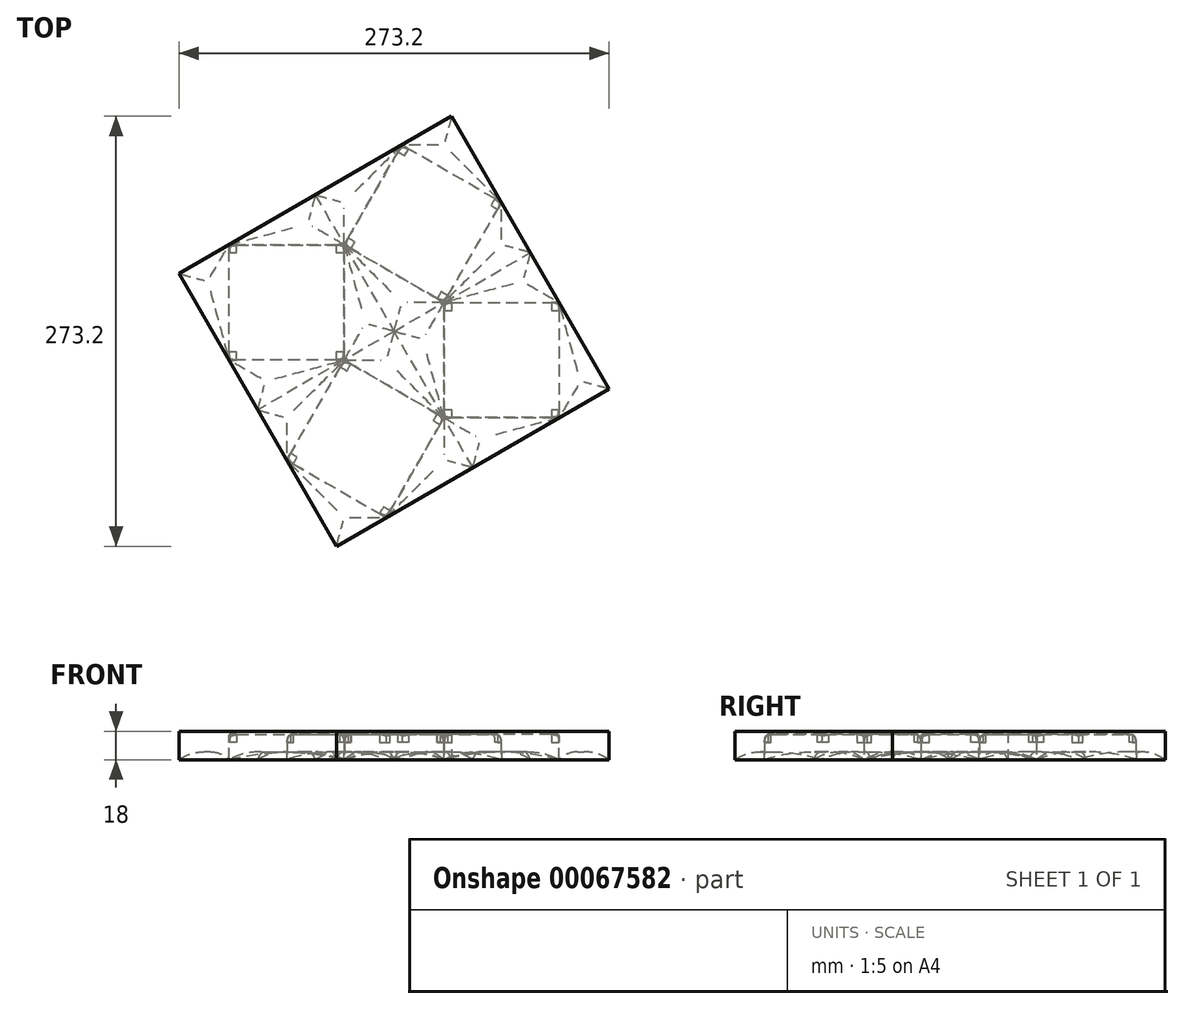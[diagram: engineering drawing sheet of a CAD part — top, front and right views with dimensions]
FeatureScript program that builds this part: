
annotation { "Feature Type Name" : "Feature", "Feature Type Description" : "" }
export const myFeature = defineFeature(function(context is Context, id is Id, definition is map)
    precondition{}
    {
        {
            var Q0;
            Q0=qCreatedBy(makeId("Top.planeOp"),FACE);
            var sketch = newSketch(context, id + "F0", { "sketchPlane" : qUnion([Q0])});
            skLineSegment(sketch, "E0.rect.bottom", {"start": v(36.6, -36.6) * mm, "end": v(-36.6, -36.6) * mm});
            skLineSegment(sketch, "E0.rect.top", {"start": v(36.6, 36.6) * mm, "end": v(-36.6, 36.6) * mm});
            skLineSegment(sketch, "E0.rect.left", {"start": v(36.6, -36.6) * mm, "end": v(36.6, 36.6) * mm});
            skLineSegment(sketch, "E0.rect.right", {"start": v(-36.6, -36.6) * mm, "end": v(-36.6, 36.6) * mm});
            skPoint(sketch, "E0.rect.middle", {"position": v(0, 0) * mm});
            skLineSegment(sketch, "E1", {"start": v(36.6, 36.6) * mm, "end": v(68.3, -18.3) * mm});
            skLineSegment(sketch, "E2", {"start": v(68.3, -18.3) * mm, "end": v(36.6, -36.6) * mm});
            skLineSegment(sketch, "E3.1.0", {"start": v(18.3, 68.3) * mm, "end": v(36.6, 36.6) * mm});
            skLineSegment(sketch, "E3.1.1", {"start": v(-36.6, 36.6) * mm, "end": v(18.3, 68.3) * mm});
            skLineSegment(sketch, "E3.2.0", {"start": v(-68.3, 18.3) * mm, "end": v(-36.6, 36.6) * mm});
            skLineSegment(sketch, "E3.2.1", {"start": v(-36.6, -36.6) * mm, "end": v(-68.3, 18.3) * mm});
            skLineSegment(sketch, "E3.3.0", {"start": v(-18.3, -68.3) * mm, "end": v(-36.6, -36.6) * mm});
            skLineSegment(sketch, "E3.3.1", {"start": v(36.6, -36.6) * mm, "end": v(-18.3, -68.3) * mm});
            skSolve(sketch);
        }
        {
            var Q0;
            Q0=makeQuery(id+"F0.imprint","IMPRINT",FACE,{"disambiguationData":[TD([[makeQuery(id+"F0.imprint","IMPRINT",EDGE,{"derivedFrom":sQuery(id+"F0.wireOp",EDGE,"E0.rect.bottom")}),-1.0]])]});
            extrude(context, id + "F1", {"entities" : qUnion([Q0]), "depth" : 16 * mm});
        }
        {
            var Q0;
            Q0=makeQuery(id+"F0.imprint","IMPRINT",FACE,{"disambiguationData":[TD([[makeQuery(id+"F0.imprint","IMPRINT",EDGE,{"derivedFrom":sQuery(id+"F0.wireOp",EDGE,"E0.rect.right")}),1.0]])]});
            var Q1;
            Q1=makeQuery(id+"F0.imprint","IMPRINT",FACE,{"disambiguationData":[TD([[makeQuery(id+"F0.imprint","IMPRINT",EDGE,{"derivedFrom":sQuery(id+"F0.wireOp",EDGE,"E0.rect.top")}),-1.0]])]});
            var Q2;
            Q2=makeQuery(id+"F0.imprint","IMPRINT",FACE,{"disambiguationData":[TD([[makeQuery(id+"F0.imprint","IMPRINT",EDGE,{"derivedFrom":sQuery(id+"F0.wireOp",EDGE,"E0.rect.left")}),-1.0]])]});
            var Q3;
            Q3=makeQuery(id+"F0.imprint","IMPRINT",FACE,{"disambiguationData":[TD([[makeQuery(id+"F0.imprint","IMPRINT",EDGE,{"derivedFrom":sQuery(id+"F0.wireOp",EDGE,"E0.rect.bottom")}),1.0]])]});
            extrude(context, id + "F2", {"entities" : qUnion([Q0, Q1, Q2, Q3]), "depth" : 5 * mm});
        }
        {
            var Q0;
            Q0=makeQuery(id+"F2.opExtrude","CAP_FACE",FACE,{"disambiguationData":[OSD([sQuery(id+"F0.wireOp",EDGE,"E0.rect.right"),sQuery(id+"F0.wireOp",EDGE,"E3.2.0"),sQuery(id+"F0.wireOp",EDGE,"E3.2.1")])],"isStart":false});
            var Q1;
            Q1=makeQuery(id+"F2.opExtrude","CAP_FACE",FACE,{"disambiguationData":[OSD([sQuery(id+"F0.wireOp",EDGE,"E0.rect.top"),sQuery(id+"F0.wireOp",EDGE,"E3.1.0"),sQuery(id+"F0.wireOp",EDGE,"E3.1.1")])],"isStart":false});
            var Q2;
            Q2=makeQuery(id+"F2.opExtrude","CAP_FACE",FACE,{"disambiguationData":[OSD([sQuery(id+"F0.wireOp",EDGE,"E0.rect.left"),sQuery(id+"F0.wireOp",EDGE,"E1"),sQuery(id+"F0.wireOp",EDGE,"E2")])],"isStart":false});
            var Q3;
            Q3=makeQuery(id+"F2.opExtrude","CAP_FACE",FACE,{"disambiguationData":[OSD([sQuery(id+"F0.wireOp",EDGE,"E0.rect.bottom"),sQuery(id+"F0.wireOp",EDGE,"E3.3.0"),sQuery(id+"F0.wireOp",EDGE,"E3.3.1")])],"isStart":false});
            fillet(context, id + "F3", {"entities" : qUnion([Q0, Q1, Q2, Q3]), "radius" : 16.26 * mm, "tangentPropagation" : true, "allowEdgeOverflow" : false});
        }
        {
            var Q0;
            Q0=makeQuery(id+"F1.opExtrude","CAP_EDGE",EDGE,{"disambiguationData":[OSD([sQuery(id+"F0.wireOp",EDGE,"E0.rect.bottom")])],"isStart":false});
            var Q1;
            Q1=makeQuery(id+"F1.opExtrude","CAP_EDGE",EDGE,{"disambiguationData":[OSD([sQuery(id+"F0.wireOp",EDGE,"E0.rect.right")])],"isStart":false});
            var Q2;
            Q2=makeQuery(id+"F1.opExtrude","CAP_EDGE",EDGE,{"disambiguationData":[OSD([sQuery(id+"F0.wireOp",EDGE,"E0.rect.top")])],"isStart":false});
            var Q3;
            Q3=makeQuery(id+"F1.opExtrude","CAP_EDGE",EDGE,{"disambiguationData":[OSD([sQuery(id+"F0.wireOp",EDGE,"E0.rect.left")])],"isStart":false});
            var Q4;
            Q4=makeQuery(id+"F1.opExtrude","SWEPT_EDGE",EDGE,{"disambiguationData":[OSD([sQuery(id+"F0.wireOp",EDGE,"E0.rect.bottom"),sQuery(id+"F0.wireOp",EDGE,"E0.rect.left"),sQuery(id+"F0.wireOp",EDGE,"E2"),sQuery(id+"F0.wireOp",EDGE,"E3.3.1")])]});
            var Q5;
            Q5=makeQuery(id+"F1.opExtrude","SWEPT_EDGE",EDGE,{"disambiguationData":[OSD([sQuery(id+"F0.wireOp",EDGE,"E0.rect.bottom"),sQuery(id+"F0.wireOp",EDGE,"E0.rect.right"),sQuery(id+"F0.wireOp",EDGE,"E3.2.1"),sQuery(id+"F0.wireOp",EDGE,"E3.3.0")])]});
            var Q6;
            Q6=makeQuery(id+"F1.opExtrude","SWEPT_EDGE",EDGE,{"disambiguationData":[OSD([sQuery(id+"F0.wireOp",EDGE,"E0.rect.top"),sQuery(id+"F0.wireOp",EDGE,"E0.rect.right"),sQuery(id+"F0.wireOp",EDGE,"E3.1.1"),sQuery(id+"F0.wireOp",EDGE,"E3.2.0")])]});
            var Q7;
            Q7=makeQuery(id+"F1.opExtrude","SWEPT_EDGE",EDGE,{"disambiguationData":[OSD([sQuery(id+"F0.wireOp",EDGE,"E0.rect.top"),sQuery(id+"F0.wireOp",EDGE,"E0.rect.left"),sQuery(id+"F0.wireOp",EDGE,"E1"),sQuery(id+"F0.wireOp",EDGE,"E3.1.0")])]});
            fillet(context, id + "F4", {"entities" : qUnion([Q0, Q1, Q2, Q3, Q4, Q5, Q6, Q7]), "radius" : 5 * mm, "tangentPropagation" : true, "rho" : 0.9, "crossSection" : FilletCrossSection.CONIC, "allowEdgeOverflow" : false});
        }
        {
            var Q0;
            Q0=sQuery(id+"F0.wireOp",EDGE,"E3.3.1");
            cPlane(context, id + "F5", {"entities" : qUnion([Q0]), "cplaneType" : CPlaneType.LINE_ANGLE, "offset" : 150 * mm, "angle" : 0 * degree, "width" : 150 * mm, "height" : 150 * mm});
        }
        {
            var Q0;
            Q0=makeQuery(id+"F1.opExtrude","SWEPT_BODY",BODY,{"disambiguationData":[OSD([sQuery(id+"F0.wireOp",EDGE,"E0.rect.bottom"),sQuery(id+"F0.wireOp",EDGE,"E0.rect.top"),sQuery(id+"F0.wireOp",EDGE,"E0.rect.left"),sQuery(id+"F0.wireOp",EDGE,"E0.rect.right")])]});
            var Q1;
            Q1=makeQuery(id+"F2.opExtrude","SWEPT_BODY",BODY,{"disambiguationData":[OSD([sQuery(id+"F0.wireOp",EDGE,"E0.rect.right"),sQuery(id+"F0.wireOp",EDGE,"E3.2.0"),sQuery(id+"F0.wireOp",EDGE,"E3.2.1")])]});
            var Q2;
            Q2=makeQuery(id+"F2.opExtrude","SWEPT_BODY",BODY,{"disambiguationData":[OSD([sQuery(id+"F0.wireOp",EDGE,"E0.rect.top"),sQuery(id+"F0.wireOp",EDGE,"E3.1.0"),sQuery(id+"F0.wireOp",EDGE,"E3.1.1")])]});
            var Q3;
            Q3=makeQuery(id+"F2.opExtrude","SWEPT_BODY",BODY,{"disambiguationData":[OSD([sQuery(id+"F0.wireOp",EDGE,"E0.rect.left"),sQuery(id+"F0.wireOp",EDGE,"E1"),sQuery(id+"F0.wireOp",EDGE,"E2")])]});
            var Q4;
            Q4=makeQuery(id+"F2.opExtrude","SWEPT_BODY",BODY,{"disambiguationData":[OSD([sQuery(id+"F0.wireOp",EDGE,"E0.rect.bottom"),sQuery(id+"F0.wireOp",EDGE,"E3.3.0"),sQuery(id+"F0.wireOp",EDGE,"E3.3.1")])]});
            var Q5;
            Q5=qCreatedBy(id+"F5.planeOp",FACE);
            mirror(context, id + "F6", {"entities" : qUnion([Q0, Q1, Q2, Q3, Q4]), "mirrorPlane" : qUnion([Q5])});
        }
        {
            var Q0;
            {var subQ0=sQuery(id+"F0.wireOp",EDGE,"E3.1.0");Q0=makeQuery(id+"F6.opPattern","COPY",EDGE,{"derivedFrom":makeQuery(id+"F3.opFillet","BLEND_EDGE",EDGE,{"blendedFrom":[makeQuery(id+"F2.opExtrude","CAP_EDGE",EDGE,{"disambiguationData":[OSD([subQ0])],"isStart":false}),makeQuery(id+"F2.opExtrude","CAP_FACE",FACE,{"disambiguationData":[OSD([sQuery(id+"F0.wireOp",EDGE,"E0.rect.top"),subQ0,sQuery(id+"F0.wireOp",EDGE,"E3.1.1")])],"isStart":true})],"blendedInto":[makeQuery(id+"F2.opExtrude","CAP_FACE",FACE,{"disambiguationData":[OSD([sQuery(id+"F0.wireOp",EDGE,"E0.rect.top"),subQ0,sQuery(id+"F0.wireOp",EDGE,"E3.1.1")])],"isStart":true})]}),"instanceName":"1"});}
            cPlane(context, id + "F7", {"entities" : qUnion([Q0]), "cplaneType" : CPlaneType.LINE_ANGLE, "offset" : 150 * mm, "angle" : 90 * degree, "width" : 150 * mm, "height" : 150 * mm});
        }
        {
            var Q0;
            Q0=makeQuery(id+"F2.opExtrude","SWEPT_BODY",BODY,{"disambiguationData":[OSD([sQuery(id+"F0.wireOp",EDGE,"E0.rect.top"),sQuery(id+"F0.wireOp",EDGE,"E3.1.0"),sQuery(id+"F0.wireOp",EDGE,"E3.1.1")])]});
            var Q1;
            Q1=makeQuery(id+"F2.opExtrude","SWEPT_BODY",BODY,{"disambiguationData":[OSD([sQuery(id+"F0.wireOp",EDGE,"E0.rect.left"),sQuery(id+"F0.wireOp",EDGE,"E1"),sQuery(id+"F0.wireOp",EDGE,"E2")])]});
            var Q2;
            Q2=makeQuery(id+"F6.opPattern","COPY",BODY,{"derivedFrom":makeQuery(id+"F2.opExtrude","SWEPT_BODY",BODY,{"disambiguationData":[OSD([sQuery(id+"F0.wireOp",EDGE,"E0.rect.left"),sQuery(id+"F0.wireOp",EDGE,"E1"),sQuery(id+"F0.wireOp",EDGE,"E2")])]}),"instanceName":"1"});
            var Q3;
            Q3=makeQuery(id+"F6.opPattern","COPY",BODY,{"derivedFrom":makeQuery(id+"F2.opExtrude","SWEPT_BODY",BODY,{"disambiguationData":[OSD([sQuery(id+"F0.wireOp",EDGE,"E0.rect.top"),sQuery(id+"F0.wireOp",EDGE,"E3.1.0"),sQuery(id+"F0.wireOp",EDGE,"E3.1.1")])]}),"instanceName":"1"});
            var Q4;
            Q4=makeQuery(id+"F6.opPattern","COPY",BODY,{"derivedFrom":makeQuery(id+"F1.opExtrude","SWEPT_BODY",BODY,{"disambiguationData":[OSD([sQuery(id+"F0.wireOp",EDGE,"E0.rect.bottom"),sQuery(id+"F0.wireOp",EDGE,"E0.rect.top"),sQuery(id+"F0.wireOp",EDGE,"E0.rect.left"),sQuery(id+"F0.wireOp",EDGE,"E0.rect.right")])]}),"instanceName":"1"});
            var Q5;
            Q5=makeQuery(id+"F1.opExtrude","SWEPT_BODY",BODY,{"disambiguationData":[OSD([sQuery(id+"F0.wireOp",EDGE,"E0.rect.bottom"),sQuery(id+"F0.wireOp",EDGE,"E0.rect.top"),sQuery(id+"F0.wireOp",EDGE,"E0.rect.left"),sQuery(id+"F0.wireOp",EDGE,"E0.rect.right")])]});
            var Q6;
            Q6=makeQuery(id+"F2.opExtrude","SWEPT_BODY",BODY,{"disambiguationData":[OSD([sQuery(id+"F0.wireOp",EDGE,"E0.rect.right"),sQuery(id+"F0.wireOp",EDGE,"E3.2.0"),sQuery(id+"F0.wireOp",EDGE,"E3.2.1")])]});
            var Q7;
            Q7=makeQuery(id+"F2.opExtrude","SWEPT_BODY",BODY,{"disambiguationData":[OSD([sQuery(id+"F0.wireOp",EDGE,"E0.rect.bottom"),sQuery(id+"F0.wireOp",EDGE,"E3.3.0"),sQuery(id+"F0.wireOp",EDGE,"E3.3.1")])]});
            var Q8;
            Q8=makeQuery(id+"F6.opPattern","COPY",BODY,{"derivedFrom":makeQuery(id+"F2.opExtrude","SWEPT_BODY",BODY,{"disambiguationData":[OSD([sQuery(id+"F0.wireOp",EDGE,"E0.rect.bottom"),sQuery(id+"F0.wireOp",EDGE,"E3.3.0"),sQuery(id+"F0.wireOp",EDGE,"E3.3.1")])]}),"instanceName":"1"});
            var Q9;
            Q9=makeQuery(id+"F6.opPattern","COPY",BODY,{"derivedFrom":makeQuery(id+"F2.opExtrude","SWEPT_BODY",BODY,{"disambiguationData":[OSD([sQuery(id+"F0.wireOp",EDGE,"E0.rect.right"),sQuery(id+"F0.wireOp",EDGE,"E3.2.0"),sQuery(id+"F0.wireOp",EDGE,"E3.2.1")])]}),"instanceName":"1"});
            var Q10;
            Q10=qCreatedBy(id+"F7.planeOp",FACE);
            mirror(context, id + "F8", {"entities" : qUnion([Q0, Q1, Q2, Q3, Q4, Q5, Q6, Q7, Q8, Q9]), "mirrorPlane" : qUnion([Q10])});
        }
        {
            var Q0;
            Q0=qCreatedBy(makeId("Top.planeOp"),FACE);
            var sketch = newSketch(context, id + "F9", { "sketchPlane" : qUnion([Q0])});
            skLineSegment(sketch, "E4", {"start": v(-68.3, 18.3) * mm, "end": v(104.9, 118.3) * mm});
            skLineSegment(sketch, "E5", {"start": v(104.9, 118.3) * mm, "end": v(204.9, -54.9) * mm});
            skLineSegment(sketch, "E6", {"start": v(204.9, -54.9) * mm, "end": v(31.7, -154.9) * mm});
            skLineSegment(sketch, "E7", {"start": v(31.7, -154.9) * mm, "end": v(-68.3, 18.3) * mm});
            skSolve(sketch);
        }
        {
            var Q0;
            Q0 = qSketchRegion(id + "F9", true);
            extrude(context, id + "F10", {"entities" : qUnion([Q0]), "depth" : 18 * mm});
        }
        {
            var Q0;
            Q0=makeQuery(id+"F1.opExtrude","SWEPT_BODY",BODY,{"disambiguationData":[OSD([sQuery(id+"F0.wireOp",EDGE,"E0.rect.bottom"),sQuery(id+"F0.wireOp",EDGE,"E0.rect.top"),sQuery(id+"F0.wireOp",EDGE,"E0.rect.left"),sQuery(id+"F0.wireOp",EDGE,"E0.rect.right")])]});
            var Q1;
            Q1=makeQuery(id+"F2.opExtrude","SWEPT_BODY",BODY,{"disambiguationData":[OSD([sQuery(id+"F0.wireOp",EDGE,"E0.rect.bottom"),sQuery(id+"F0.wireOp",EDGE,"E3.3.0"),sQuery(id+"F0.wireOp",EDGE,"E3.3.1")])]});
            var Q2;
            Q2=makeQuery(id+"F2.opExtrude","SWEPT_BODY",BODY,{"disambiguationData":[OSD([sQuery(id+"F0.wireOp",EDGE,"E0.rect.top"),sQuery(id+"F0.wireOp",EDGE,"E3.1.0"),sQuery(id+"F0.wireOp",EDGE,"E3.1.1")])]});
            var Q3;
            Q3=makeQuery(id+"F2.opExtrude","SWEPT_BODY",BODY,{"disambiguationData":[OSD([sQuery(id+"F0.wireOp",EDGE,"E0.rect.left"),sQuery(id+"F0.wireOp",EDGE,"E1"),sQuery(id+"F0.wireOp",EDGE,"E2")])]});
            var Q4;
            Q4=makeQuery(id+"F2.opExtrude","SWEPT_BODY",BODY,{"disambiguationData":[OSD([sQuery(id+"F0.wireOp",EDGE,"E0.rect.right"),sQuery(id+"F0.wireOp",EDGE,"E3.2.0"),sQuery(id+"F0.wireOp",EDGE,"E3.2.1")])]});
            var Q5;
            Q5=makeQuery(id+"F6.opPattern","COPY",BODY,{"derivedFrom":makeQuery(id+"F1.opExtrude","SWEPT_BODY",BODY,{"disambiguationData":[OSD([sQuery(id+"F0.wireOp",EDGE,"E0.rect.bottom"),sQuery(id+"F0.wireOp",EDGE,"E0.rect.top"),sQuery(id+"F0.wireOp",EDGE,"E0.rect.left"),sQuery(id+"F0.wireOp",EDGE,"E0.rect.right")])]}),"instanceName":"1"});
            var Q6;
            Q6=makeQuery(id+"F6.opPattern","COPY",BODY,{"derivedFrom":makeQuery(id+"F2.opExtrude","SWEPT_BODY",BODY,{"disambiguationData":[OSD([sQuery(id+"F0.wireOp",EDGE,"E0.rect.bottom"),sQuery(id+"F0.wireOp",EDGE,"E3.3.0"),sQuery(id+"F0.wireOp",EDGE,"E3.3.1")])]}),"instanceName":"1"});
            var Q7;
            Q7=makeQuery(id+"F6.opPattern","COPY",BODY,{"derivedFrom":makeQuery(id+"F2.opExtrude","SWEPT_BODY",BODY,{"disambiguationData":[OSD([sQuery(id+"F0.wireOp",EDGE,"E0.rect.top"),sQuery(id+"F0.wireOp",EDGE,"E3.1.0"),sQuery(id+"F0.wireOp",EDGE,"E3.1.1")])]}),"instanceName":"1"});
            var Q8;
            Q8=makeQuery(id+"F6.opPattern","COPY",BODY,{"derivedFrom":makeQuery(id+"F2.opExtrude","SWEPT_BODY",BODY,{"disambiguationData":[OSD([sQuery(id+"F0.wireOp",EDGE,"E0.rect.left"),sQuery(id+"F0.wireOp",EDGE,"E1"),sQuery(id+"F0.wireOp",EDGE,"E2")])]}),"instanceName":"1"});
            var Q9;
            Q9=makeQuery(id+"F6.opPattern","COPY",BODY,{"derivedFrom":makeQuery(id+"F2.opExtrude","SWEPT_BODY",BODY,{"disambiguationData":[OSD([sQuery(id+"F0.wireOp",EDGE,"E0.rect.right"),sQuery(id+"F0.wireOp",EDGE,"E3.2.0"),sQuery(id+"F0.wireOp",EDGE,"E3.2.1")])]}),"instanceName":"1"});
            var Q10;
            Q10=makeQuery(id+"F8.opPattern","COPY",BODY,{"derivedFrom":makeQuery(id+"F1.opExtrude","SWEPT_BODY",BODY,{"disambiguationData":[OSD([sQuery(id+"F0.wireOp",EDGE,"E0.rect.bottom"),sQuery(id+"F0.wireOp",EDGE,"E0.rect.top"),sQuery(id+"F0.wireOp",EDGE,"E0.rect.left"),sQuery(id+"F0.wireOp",EDGE,"E0.rect.right")])]}),"instanceName":"1"});
            var Q11;
            Q11=makeQuery(id+"F8.opPattern","COPY",BODY,{"derivedFrom":makeQuery(id+"F2.opExtrude","SWEPT_BODY",BODY,{"disambiguationData":[OSD([sQuery(id+"F0.wireOp",EDGE,"E0.rect.bottom"),sQuery(id+"F0.wireOp",EDGE,"E3.3.0"),sQuery(id+"F0.wireOp",EDGE,"E3.3.1")])]}),"instanceName":"1"});
            var Q12;
            Q12=makeQuery(id+"F8.opPattern","COPY",BODY,{"derivedFrom":makeQuery(id+"F2.opExtrude","SWEPT_BODY",BODY,{"disambiguationData":[OSD([sQuery(id+"F0.wireOp",EDGE,"E0.rect.top"),sQuery(id+"F0.wireOp",EDGE,"E3.1.0"),sQuery(id+"F0.wireOp",EDGE,"E3.1.1")])]}),"instanceName":"1"});
            var Q13;
            Q13=makeQuery(id+"F8.opPattern","COPY",BODY,{"derivedFrom":makeQuery(id+"F2.opExtrude","SWEPT_BODY",BODY,{"disambiguationData":[OSD([sQuery(id+"F0.wireOp",EDGE,"E0.rect.left"),sQuery(id+"F0.wireOp",EDGE,"E1"),sQuery(id+"F0.wireOp",EDGE,"E2")])]}),"instanceName":"1"});
            var Q14;
            Q14=makeQuery(id+"F8.opPattern","COPY",BODY,{"derivedFrom":makeQuery(id+"F2.opExtrude","SWEPT_BODY",BODY,{"disambiguationData":[OSD([sQuery(id+"F0.wireOp",EDGE,"E0.rect.right"),sQuery(id+"F0.wireOp",EDGE,"E3.2.0"),sQuery(id+"F0.wireOp",EDGE,"E3.2.1")])]}),"instanceName":"1"});
            var Q15;
            Q15=makeQuery(id+"F8.opPattern","COPY",BODY,{"derivedFrom":makeQuery(id+"F6.opPattern","COPY",BODY,{"derivedFrom":makeQuery(id+"F1.opExtrude","SWEPT_BODY",BODY,{"disambiguationData":[OSD([sQuery(id+"F0.wireOp",EDGE,"E0.rect.bottom"),sQuery(id+"F0.wireOp",EDGE,"E0.rect.top"),sQuery(id+"F0.wireOp",EDGE,"E0.rect.left"),sQuery(id+"F0.wireOp",EDGE,"E0.rect.right")])]}),"instanceName":"1"}),"instanceName":"1"});
            var Q16;
            Q16=makeQuery(id+"F8.opPattern","COPY",BODY,{"derivedFrom":makeQuery(id+"F6.opPattern","COPY",BODY,{"derivedFrom":makeQuery(id+"F2.opExtrude","SWEPT_BODY",BODY,{"disambiguationData":[OSD([sQuery(id+"F0.wireOp",EDGE,"E0.rect.bottom"),sQuery(id+"F0.wireOp",EDGE,"E3.3.0"),sQuery(id+"F0.wireOp",EDGE,"E3.3.1")])]}),"instanceName":"1"}),"instanceName":"1"});
            var Q17;
            Q17=makeQuery(id+"F8.opPattern","COPY",BODY,{"derivedFrom":makeQuery(id+"F6.opPattern","COPY",BODY,{"derivedFrom":makeQuery(id+"F2.opExtrude","SWEPT_BODY",BODY,{"disambiguationData":[OSD([sQuery(id+"F0.wireOp",EDGE,"E0.rect.top"),sQuery(id+"F0.wireOp",EDGE,"E3.1.0"),sQuery(id+"F0.wireOp",EDGE,"E3.1.1")])]}),"instanceName":"1"}),"instanceName":"1"});
            var Q18;
            Q18=makeQuery(id+"F8.opPattern","COPY",BODY,{"derivedFrom":makeQuery(id+"F6.opPattern","COPY",BODY,{"derivedFrom":makeQuery(id+"F2.opExtrude","SWEPT_BODY",BODY,{"disambiguationData":[OSD([sQuery(id+"F0.wireOp",EDGE,"E0.rect.left"),sQuery(id+"F0.wireOp",EDGE,"E1"),sQuery(id+"F0.wireOp",EDGE,"E2")])]}),"instanceName":"1"}),"instanceName":"1"});
            var Q19;
            Q19=makeQuery(id+"F8.opPattern","COPY",BODY,{"derivedFrom":makeQuery(id+"F6.opPattern","COPY",BODY,{"derivedFrom":makeQuery(id+"F2.opExtrude","SWEPT_BODY",BODY,{"disambiguationData":[OSD([sQuery(id+"F0.wireOp",EDGE,"E0.rect.right"),sQuery(id+"F0.wireOp",EDGE,"E3.2.0"),sQuery(id+"F0.wireOp",EDGE,"E3.2.1")])]}),"instanceName":"1"}),"instanceName":"1"});
            var Q20;
            Q20=makeQuery(id+"F10.opExtrude","SWEPT_BODY",BODY,{"disambiguationData":[OSD([sQuery(id+"F9.wireOp",EDGE,"E4"),sQuery(id+"F9.wireOp",EDGE,"E5"),sQuery(id+"F9.wireOp",EDGE,"E6"),sQuery(id+"F9.wireOp",EDGE,"E7")])]});
            booleanBodies(context, id + "F11", {"operationType" : BooleanOperationType.SUBTRACTION, "tools" : qUnion([Q0, Q1, Q2, Q3, Q4, Q5, Q6, Q7, Q8, Q9, Q10, Q11, Q12, Q13, Q14, Q15, Q16, Q17, Q18, Q19]), "targets" : qUnion([Q20])});
        }
    });
